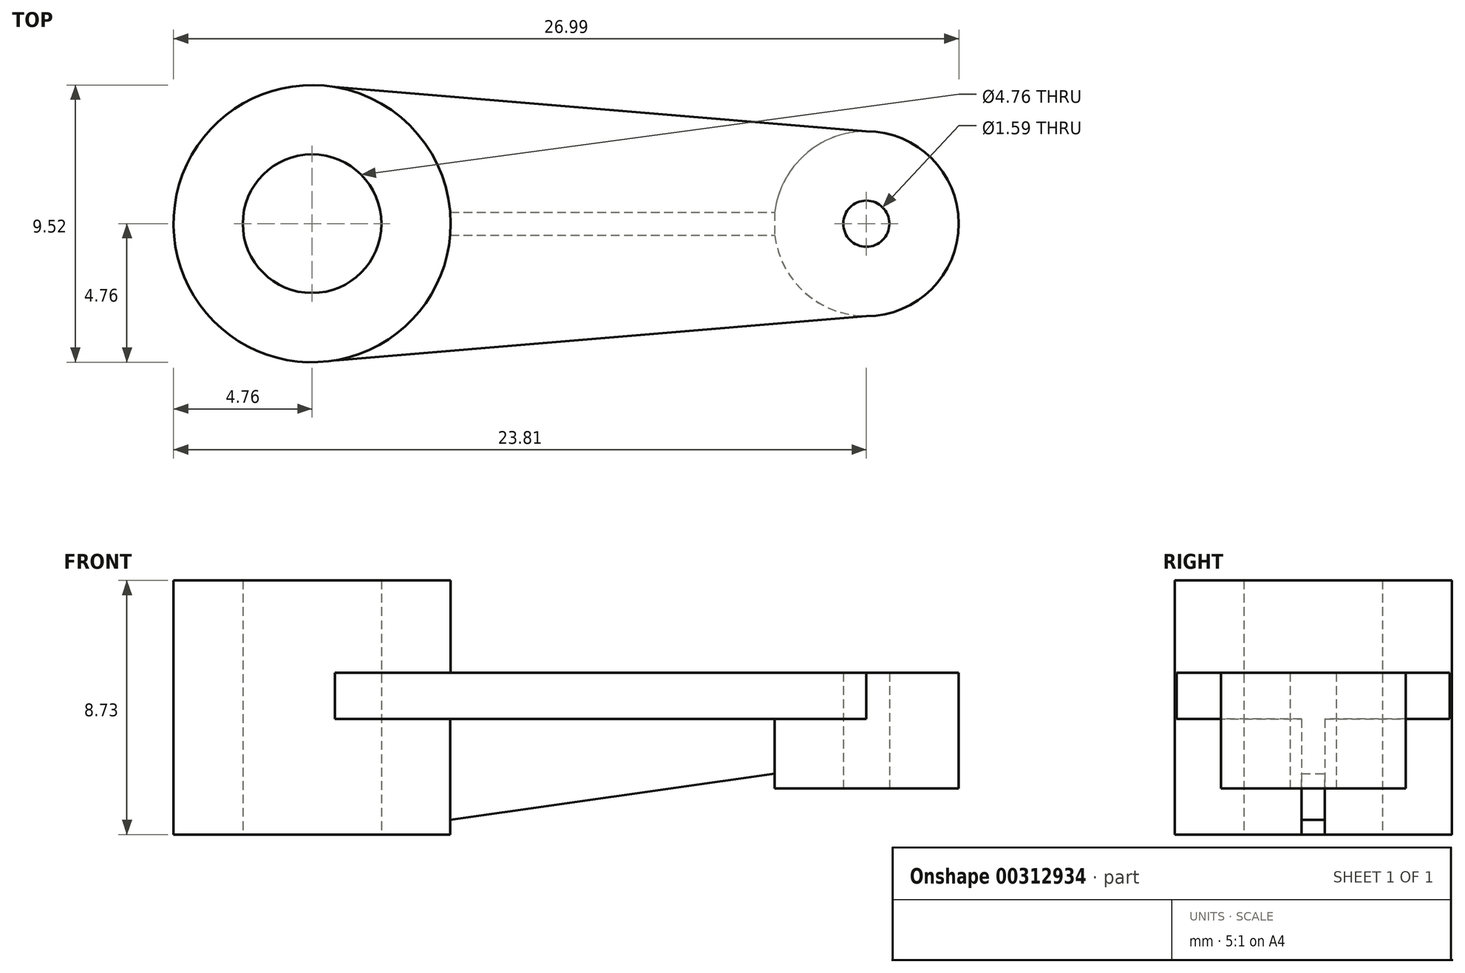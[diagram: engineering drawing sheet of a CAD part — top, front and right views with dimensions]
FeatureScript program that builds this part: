
annotation { "Feature Type Name" : "Feature", "Feature Type Description" : "" }
export const myFeature = defineFeature(function(context is Context, id is Id, definition is map)
    precondition{}
    {
        {
            var Q0;
            Q0=qCreatedBy(makeId("Top.planeOp"),FACE);
            var sketch = newSketch(context, id + "F0", { "sketchPlane" : qUnion([Q0])});
            skCircle(sketch, "E0", {"center": v(0, 0) * mm, "radius": 4.76 * mm});
            skCircle(sketch, "E1", {"center": v(19.05, 0) * mm, "radius": 3.18 * mm});
            skLineSegment(sketch, "E2", {"start": v(0, 0) * mm, "end": v(0, -4.76) * mm});
            skLineSegment(sketch, "E3", {"start": v(0, -4.76) * mm, "end": v(19.05, -3.17) * mm});
            skLineSegment(sketch, "E4", {"start": v(19.05, -3.17) * mm, "end": v(19.05, 0) * mm});
            skLineSegment(sketch, "E5", {"start": v(19.05, 3.17) * mm, "end": v(0, 4.76) * mm});
            skCircle(sketch, "E6", {"center": v(0, 0) * mm, "radius": 2.38 * mm});
            skCircle(sketch, "E7", {"center": v(19.05, 0) * mm, "radius": 0.8 * mm});
            skSolve(sketch);
        }
        {
            var Q0;
            Q0 = qSketchRegion(id + "F0", true);
            extrude(context, id + "F1", {"entities" : qUnion([Q0]), "depth" : 1.59 * mm});
        }
        {
            var Q0;
            Q0=makeQuery(id+"F1.opExtrude","CAP_FACE",FACE,{"disambiguationData":[OSD([sQuery(id+"F0.wireOp",EDGE,"E0"),sQuery(id+"F0.wireOp",EDGE,"E1"),sQuery(id+"F0.wireOp",EDGE,"E3"),sQuery(id+"F0.wireOp",EDGE,"E5"),sQuery(id+"F0.wireOp",EDGE,"E6"),sQuery(id+"F0.wireOp",EDGE,"E7")])],"isStart":false});
            var sketch = newSketch(context, id + "F2", { "sketchPlane" : qUnion([Q0])});
            skCircle(sketch, "E8", {"center": v(0, 0) * mm, "radius": 4.76 * mm});
            skCircle(sketch, "E9", {"center": v(0, 0) * mm, "radius": 2.38 * mm});
            skSolve(sketch);
        }
        {
            var Q0;
            Q0 = qSketchRegion(id + "F2", true);
            extrude(context, id + "F3", {"entities" : qUnion([Q0]), "operationType" : NewBodyOperationType.ADD, "depth" : 3.17 * mm});
        }
        {
            var Q0;
            Q0=makeQuery(id+"F1.opExtrude","CAP_FACE",FACE,{"disambiguationData":[OSD([sQuery(id+"F0.wireOp",EDGE,"E0"),sQuery(id+"F0.wireOp",EDGE,"E1"),sQuery(id+"F0.wireOp",EDGE,"E3"),sQuery(id+"F0.wireOp",EDGE,"E5"),sQuery(id+"F0.wireOp",EDGE,"E6"),sQuery(id+"F0.wireOp",EDGE,"E7")])],"isStart":true});
            var sketch = newSketch(context, id + "F4", { "sketchPlane" : qUnion([Q0])});
            skCircle(sketch, "E10", {"center": v(0, 0) * mm, "radius": 4.76 * mm});
            skCircle(sketch, "E11", {"center": v(0, 0) * mm, "radius": 2.38 * mm});
            skSolve(sketch);
        }
        {
            var Q0;
            Q0 = qSketchRegion(id + "F4", true);
            extrude(context, id + "F5", {"entities" : qUnion([Q0]), "operationType" : NewBodyOperationType.ADD, "depth" : 3.97 * mm});
        }
        {
            var Q0;
            Q0=makeQuery(id+"F1.opExtrude","CAP_FACE",FACE,{"disambiguationData":[OSD([sQuery(id+"F0.wireOp",EDGE,"E0"),sQuery(id+"F0.wireOp",EDGE,"E1"),sQuery(id+"F0.wireOp",EDGE,"E3"),sQuery(id+"F0.wireOp",EDGE,"E5"),sQuery(id+"F0.wireOp",EDGE,"E6"),sQuery(id+"F0.wireOp",EDGE,"E7")])],"isStart":true});
            var sketch = newSketch(context, id + "F6", { "sketchPlane" : qUnion([Q0])});
            skCircle(sketch, "E12", {"center": v(19.05, 0) * mm, "radius": 3.18 * mm});
            skCircle(sketch, "E13", {"center": v(19.05, 0) * mm, "radius": 0.8 * mm});
            skSolve(sketch);
        }
        {
            var Q0;
            Q0 = qSketchRegion(id + "F6", true);
            extrude(context, id + "F7", {"entities" : qUnion([Q0]), "operationType" : NewBodyOperationType.ADD, "depth" : 2.38 * mm});
        }
        {
            var Q0;
            Q0=makeQuery(id+"F5.opExtrude","CAP_FACE",FACE,{"disambiguationData":[OSD([sQuery(id+"F4.wireOp",EDGE,"E10"),sQuery(id+"F4.wireOp",EDGE,"E11")])],"isStart":false});
            var sketch = newSketch(context, id + "F8", { "sketchPlane" : qUnion([Q0])});
            skCircle(sketch, "E14", {"center": v(0, 0) * mm, "radius": 4.76 * mm});
            skCircle(sketch, "E15", {"center": v(19.05, 0) * mm, "radius": 3.18 * mm});
            skLineSegment(sketch, "E16", {"start": v(4.75, 0.4) * mm, "end": v(15.9, 0.4) * mm});
            skLineSegment(sketch, "E17", {"start": v(15.9, -0.4) * mm, "end": v(4.75, -0.4) * mm});
            skSolve(sketch);
        }
        {
            var Q0;
            {var subQ0=sQuery(id+"F8.wireOp",EDGE,"E16");Q0=makeQuery(id+"F8.imprint","IMPRINT",FACE,{"disambiguationData":[TD([[makeQuery(id+"F8.imprint","IMPRINT",EDGE,{"derivedFrom":subQ0}),-1.0]])]});}
            extrude(context, id + "F9", {"entities" : qUnion([Q0]), "operationType" : NewBodyOperationType.ADD, "endBound" : BoundingType.UP_TO_NEXT, "oppositeDirection" : true, "depth" : 25.4 * mm});
        }
        {
            var Q0;
            Q0=makeQuery(id+"F9.opExtrude","SWEPT_FACE",FACE,{"disambiguationData":[OSD([sQuery(id+"F8.wireOp",EDGE,"E17")])]});
            var sketch = newSketch(context, id + "F10", { "sketchPlane" : qUnion([Q0])});
            skLineSegment(sketch, "E18", {"start": v(-4.75, -3.46) * mm, "end": v(-15.9, -1.87) * mm});
            skSolve(sketch);
        }
        {
            var Q0;
            Q0 = qSketchRegion(id + "F10", true);
            var Q1;
            {var subQ7=sQuery(id+"F10.wireOp",EDGE,"E18");Q1=makeQuery(id+"F10.imprint","IMPRINT",FACE,{"disambiguationData":[TD([[makeQuery(id+"F10.imprint","IMPRINT",EDGE,{"derivedFrom":subQ7}),1.0]])]});}
            extrude(context, id + "F11", {"entities" : qUnion([Q0, Q1]), "operationType" : NewBodyOperationType.REMOVE, "oppositeDirection" : true, "depth" : 25.4 * mm});
        }
    });
